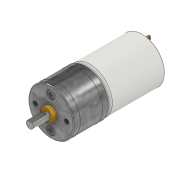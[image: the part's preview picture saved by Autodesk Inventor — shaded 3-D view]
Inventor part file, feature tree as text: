
AUTODESK INVENTOR PART (.ipt)
format: ipt  version: 2020.3 (Build 243373000, 373)  size: 392,704 bytes
history: native  units: mm
features: sketch x12, extrude x9, fillet x8, hole x2, chamfer x1, revolve x1, pattern_circular x1
ambient origin geometry x8: Origin, YZ Plane, XZ Plane, XY Plane, X Axis, Y Axis, Z Axis, Center Point
bodies: Solid1 (feature_tree), Solid2 (feature_tree), Solid3 (feature_tree), Solid4 (feature_tree), Solid5 (feature_tree), Solid6 (feature_tree)
feature tree (34):
  extrude  "Extrusion1"  Depth=30.8mm TaperAngle=0.0deg
  fillet  "Fillet1"  Radius=2.0mm
  extrude  "Extrusion2"  Depth=2.0mm
  chamfer  "Chamfer1"  Distance=1.0mm
  fillet  "Fillet3"  Radius=0.3mm
  extrude  "Extrusion3"  Depth=2.0mm TaperAngle=0.0deg
  fillet  "Fillet4"  Radius=0.5mm
  extrude  "Extrusion4"  Depth=19.2mm TaperAngle=0.0deg
  fillet  "Fillet5"  Radius=0.5mm
  extrude  "Extrusion5"  Depth=2.5mm TaperAngle=0.0deg
  extrude  "Extrusion6"  Depth=9.0mm TaperAngle=0.0deg
  extrude  "Extrusion7"  Depth=0.5mm
  revolve  "Revolution1"  [1 undecoded]
  fillet  "Fillet6"  Radius=8.0mm
  fillet  "Fillet7"  Radius=0.02mm
  hole  "Hole1"  [1 undecoded]
  hole  "Hole2"  [1 undecoded]
  extrude  "Extrusion8"  Depth=3.5mm
  fillet  "Fillet8"  [1 undecoded]
  extrude  "Extrusion9"  Depth=0.5mm
  pattern_circular  "Circular Pattern1"  [2 undecoded]
  fillet  "Fillet9"  Radius=17.0mm
  sketch  "Sketch1"  dims[d0=24.4mm d1=30.8mm d2=0.0mm d3=2.0mm]
  sketch  "Sketch2"  dims[d4=2.0mm d5=2.0mm]
  sketch  "Sketch3"  dims[d6=8.0mm]
  sketch  "Sketch4"  dims[d7=15.0mm]
  sketch  "Sketch5"  dims[d8=7.5mm]
  sketch  "Sketch6"  dims[d9=1.5mm]
  sketch  "Sketch7"  dims[d10=1.5mm d11=1.0mm d12=0.0mm]
  sketch  "Sketch8"  dims[d14=0.3mm d15=2.0mm d16=45.0deg d17=0.3mm]
  sketch  "Sketch9"  dims[d18=6.5mm d19=2.0mm d20=0.0mm d21=0.5mm]
  sketch  "Sketch10"  dims[d22=25.0mm d23=19.2mm d24=0.0mm d25=0.5mm]
  sketch  "Sketch11"  dims[d26=7.0mm d27=2.5mm d28=0.0mm]
  sketch  "Sketch12"  dims[d29=4.0mm d30=9.0mm d31=0.0mm d32=1.5mm d33=5.0mm d34=8.0mm d35=0.0mm d36=0.02mm d37=0.5mm d38=3.5mm d39=3.5mm d40=90.0deg d41=0.01mm d42=0.01mm d43=2.4mm d44=6.0mm d45=4.4mm d46=2.3mm d47=90.0deg d48=8.0mm d49=20.594885mm d50=17.0mm d51=8.5mm d52=2.459mm d53=6.0mm d54=4.4mm d55=2.3mm d56=90.0deg d57=8.8mm d58=20.594885mm d59=17.0mm d60=4.0mm d61=2.5mm d62=0.0mm d63=1.0mm d64=2.5mm d65=0.5mm d66=0.5mm d67=0.5mm d68=0.0mm d69=20.0mm d70=360.0deg d72=0.5mm]
note: 6 required parameter values undecoded (feature->parameter linkage not recoverable at this tier; creation-order binding heuristic only, values carry confidence <= 0.55)